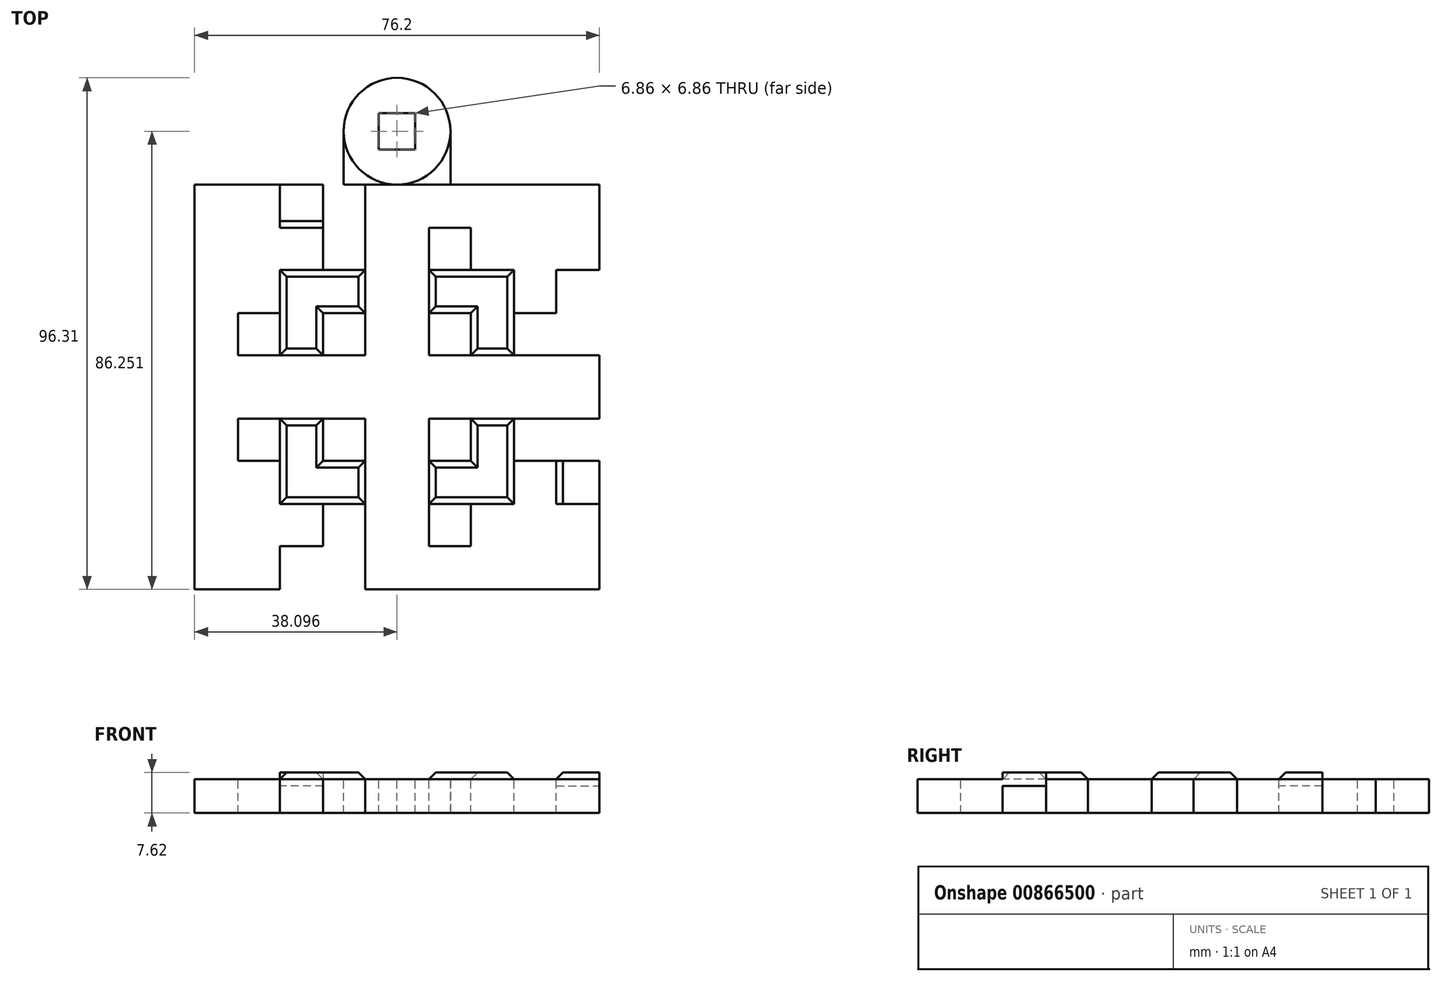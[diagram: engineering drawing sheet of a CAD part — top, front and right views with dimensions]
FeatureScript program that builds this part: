
annotation { "Feature Type Name" : "Feature", "Feature Type Description" : "" }
export const myFeature = defineFeature(function(context is Context, id is Id, definition is map)
    precondition{}
    {
        {
            var Q0;
            Q0=qCreatedBy(makeId("Top.planeOp"),FACE);
            var sketch = newSketch(context, id + "F0", { "sketchPlane" : qUnion([Q0])});
            skLineSegment(sketch, "E0.bottom", {"start": v(-34.48, 49.13) * mm, "end": v(41.72, 49.13) * mm});
            skLineSegment(sketch, "E0.top", {"start": v(-34.48, -27.07) * mm, "end": v(41.72, -27.07) * mm});
            skLineSegment(sketch, "E0.left", {"start": v(-34.48, 49.13) * mm, "end": v(-34.48, -27.07) * mm});
            skLineSegment(sketch, "E0.right", {"start": v(41.72, 49.13) * mm, "end": v(41.72, -27.07) * mm});
            skCircle(sketch, "E1", {"center": v(3.62, 59.18) * mm, "radius": 10.06 * mm});
            skLineSegment(sketch, "E2", {"start": v(3.62, -27.07) * mm, "end": v(3.62, 49.13) * mm, "construction": true});
            skPoint(sketch, "E3", {"position": v(3.62, 49.13) * mm});
            skSolve(sketch);
        }
        {
            var Q0;
            Q0=qSketchRegion(id+"F0",true);
            extrude(context, id + "F1", {"entities" : qUnion([Q0]), "depth" : 6.35 * mm, "offsetDistance" : 25.4 * mm});
        }
        {
            var Q0;
            Q0=makeQuery(id+"F1.opExtrude","CAP_FACE",FACE,{"disambiguationData":[OSD([sQuery(id+"F0.wireOp",EDGE,"E0.bottom"),sQuery(id+"F0.wireOp",EDGE,"E0.top"),sQuery(id+"F0.wireOp",EDGE,"E0.left"),sQuery(id+"F0.wireOp",EDGE,"E0.right")])],"isStart":false});
            var sketch = newSketch(context, id + "F2", { "sketchPlane" : qUnion([Q0])});
            skLineSegment(sketch, "E4.bottom", {"start": v(-34.48, 5.04) * mm, "end": v(41.72, 5.04) * mm});
            skLineSegment(sketch, "E4.top", {"start": v(-34.48, 17.01) * mm, "end": v(41.72, 17.01) * mm});
            skLineSegment(sketch, "E4.left", {"start": v(-34.48, 5.04) * mm, "end": v(-34.48, 17.01) * mm});
            skLineSegment(sketch, "E4.right", {"start": v(41.72, 5.04) * mm, "end": v(41.72, 17.01) * mm});
            skLineSegment(sketch, "E5.bottom", {"start": v(-34.48, 49.13) * mm, "end": v(-2.37, 49.13) * mm});
            skLineSegment(sketch, "E5.top", {"start": v(-34.48, -27.07) * mm, "end": v(-2.37, -27.07) * mm});
            skLineSegment(sketch, "E5.left", {"start": v(-34.48, 49.13) * mm, "end": v(-34.48, 17.01) * mm});
            skLineSegment(sketch, "E5.right", {"start": v(41.72, 49.13) * mm, "end": v(41.72, 17.01) * mm});
            skLineSegment(sketch, "E6", {"start": v(41.72, 17.01) * mm, "end": v(41.72, 5.04) * mm});
            skLineSegment(sketch, "E7", {"start": v(41.72, 5.04) * mm, "end": v(41.72, -27.07) * mm});
            skLineSegment(sketch, "E8.bottom", {"start": v(-2.37, 49.13) * mm, "end": v(9.6, 49.13) * mm});
            skLineSegment(sketch, "E8.top", {"start": v(-2.37, -27.07) * mm, "end": v(9.6, -27.07) * mm});
            skLineSegment(sketch, "E8.left", {"start": v(-2.37, 49.13) * mm, "end": v(-2.37, 49.13) * mm});
            skLineSegment(sketch, "E8.right", {"start": v(9.6, 49.13) * mm, "end": v(9.6, -27.07) * mm});
            skLineSegment(sketch, "E9", {"start": v(-2.37, 49.13) * mm, "end": v(-2.37, -27.07) * mm});
            skLineSegment(sketch, "E10", {"start": v(9.6, 49.13) * mm, "end": v(41.72, 49.13) * mm});
            skLineSegment(sketch, "E11", {"start": v(9.6, -27.07) * mm, "end": v(41.72, -27.07) * mm});
            skPoint(sketch, "E12.oppositeSnap0", {"position": v(25.66, 49.13) * mm});
            skLineSegment(sketch, "E12.bottom", {"start": v(-18.43, 49.13) * mm, "end": v(25.66, 49.13) * mm});
            skLineSegment(sketch, "E12.top", {"start": v(-18.43, 40.98) * mm, "end": v(25.66, 40.98) * mm});
            skLineSegment(sketch, "E12.left", {"start": v(-18.43, 49.13) * mm, "end": v(-18.43, 40.98) * mm});
            skLineSegment(sketch, "E12.right", {"start": v(25.66, 49.13) * mm, "end": v(25.66, 40.98) * mm});
            skPoint(sketch, "E13.oppositeSnap0", {"position": v(-18.43, -27.07) * mm});
            skLineSegment(sketch, "E13.bottom", {"start": v(25.66, -27.07) * mm, "end": v(-18.43, -27.07) * mm});
            skLineSegment(sketch, "E13.top", {"start": v(25.66, -18.92) * mm, "end": v(-18.43, -18.92) * mm});
            skLineSegment(sketch, "E13.left", {"start": v(25.66, -27.07) * mm, "end": v(25.66, -18.92) * mm});
            skLineSegment(sketch, "E13.right", {"start": v(-18.43, -27.07) * mm, "end": v(-18.43, -18.92) * mm});
            skPoint(sketch, "E14.oppositeSnap0", {"position": v(41.72, 33.07) * mm});
            skLineSegment(sketch, "E14.bottom", {"start": v(41.72, -11.02) * mm, "end": v(33.57, -11.02) * mm});
            skLineSegment(sketch, "E14.top", {"start": v(41.72, 33.07) * mm, "end": v(33.57, 33.07) * mm});
            skLineSegment(sketch, "E14.left", {"start": v(41.72, -11.02) * mm, "end": v(41.72, 33.07) * mm});
            skLineSegment(sketch, "E14.right", {"start": v(33.57, -11.02) * mm, "end": v(33.57, 33.07) * mm});
            skLineSegment(sketch, "E15", {"start": v(-34.48, 17.01) * mm, "end": v(-34.48, 5.04) * mm});
            skLineSegment(sketch, "E16", {"start": v(-34.48, 5.04) * mm, "end": v(-34.48, -27.07) * mm});
            skPoint(sketch, "E17.oppositeSnap0", {"position": v(-34.48, -11.02) * mm});
            skLineSegment(sketch, "E17.bottom", {"start": v(-34.48, 33.07) * mm, "end": v(-26.33, 33.07) * mm});
            skLineSegment(sketch, "E17.top", {"start": v(-34.48, -11.02) * mm, "end": v(-26.33, -11.02) * mm});
            skLineSegment(sketch, "E17.left", {"start": v(-34.48, 33.07) * mm, "end": v(-34.48, -11.02) * mm});
            skLineSegment(sketch, "E17.right", {"start": v(-26.33, 33.07) * mm, "end": v(-26.33, 24.92) * mm});
            skLineSegment(sketch, "E18.bottom", {"start": v(-18.43, 40.98) * mm, "end": v(-10.28, 40.98) * mm});
            skLineSegment(sketch, "E18.top", {"start": v(-18.43, 17.01) * mm, "end": v(-10.28, 17.01) * mm});
            skLineSegment(sketch, "E18.left", {"start": v(-18.43, 40.98) * mm, "end": v(-18.43, 17.01) * mm});
            skLineSegment(sketch, "E18.right", {"start": v(-10.28, 40.98) * mm, "end": v(-10.28, 17.01) * mm});
            skLineSegment(sketch, "E19.bottom", {"start": v(-26.33, 33.07) * mm, "end": v(-2.37, 33.07) * mm});
            skLineSegment(sketch, "E19.top", {"start": v(-26.33, 24.92) * mm, "end": v(-2.37, 24.92) * mm});
            skLineSegment(sketch, "E19.right", {"start": v(-2.37, 33.07) * mm, "end": v(-2.37, 24.92) * mm});
            skLineSegment(sketch, "E20", {"start": v(-26.33, 24.92) * mm, "end": v(-26.33, -11.02) * mm});
            skLineSegment(sketch, "E21.bottom", {"start": v(25.66, 40.98) * mm, "end": v(17.51, 40.98) * mm});
            skLineSegment(sketch, "E21.top", {"start": v(25.66, 17.01) * mm, "end": v(17.51, 17.01) * mm});
            skLineSegment(sketch, "E21.left", {"start": v(25.66, 40.98) * mm, "end": v(25.66, 17.01) * mm});
            skLineSegment(sketch, "E21.right", {"start": v(17.51, 40.98) * mm, "end": v(17.51, 17.01) * mm});
            skLineSegment(sketch, "E22.bottom", {"start": v(33.57, 33.07) * mm, "end": v(9.6, 33.07) * mm});
            skLineSegment(sketch, "E22.top", {"start": v(33.57, 24.92) * mm, "end": v(9.6, 24.92) * mm});
            skLineSegment(sketch, "E22.left", {"start": v(33.57, 33.07) * mm, "end": v(33.57, 24.92) * mm});
            skLineSegment(sketch, "E22.right", {"start": v(9.6, 33.07) * mm, "end": v(9.6, 24.92) * mm});
            skPoint(sketch, "E23.oppositeSnap0", {"position": v(-10.28, 29) * mm});
            skLineSegment(sketch, "E23.bottom", {"start": v(-18.43, -18.92) * mm, "end": v(-10.28, -18.92) * mm});
            skLineSegment(sketch, "E23.top", {"start": v(-18.43, 5.04) * mm, "end": v(-10.28, 5.04) * mm});
            skLineSegment(sketch, "E23.left", {"start": v(-18.43, -18.92) * mm, "end": v(-18.43, 5.04) * mm});
            skLineSegment(sketch, "E23.right", {"start": v(-10.28, -18.92) * mm, "end": v(-10.28, 5.04) * mm});
            skLineSegment(sketch, "E24.bottom", {"start": v(25.66, -18.92) * mm, "end": v(17.51, -18.92) * mm});
            skLineSegment(sketch, "E24.top", {"start": v(25.66, 5.04) * mm, "end": v(17.51, 5.04) * mm});
            skLineSegment(sketch, "E24.left", {"start": v(25.66, -18.92) * mm, "end": v(25.66, 5.04) * mm});
            skLineSegment(sketch, "E24.right", {"start": v(17.51, -18.92) * mm, "end": v(17.51, 5.04) * mm});
            skLineSegment(sketch, "E25.bottom", {"start": v(-26.33, -11.02) * mm, "end": v(-2.37, -11.02) * mm});
            skLineSegment(sketch, "E25.top", {"start": v(-26.33, -2.87) * mm, "end": v(-2.37, -2.87) * mm});
            skLineSegment(sketch, "E25.left", {"start": v(-26.33, -11.02) * mm, "end": v(-26.33, -2.87) * mm});
            skLineSegment(sketch, "E25.right", {"start": v(-2.37, -11.02) * mm, "end": v(-2.37, -2.87) * mm});
            skLineSegment(sketch, "E26.bottom", {"start": v(9.6, -11.02) * mm, "end": v(33.57, -11.02) * mm});
            skLineSegment(sketch, "E26.top", {"start": v(9.6, -2.87) * mm, "end": v(33.57, -2.87) * mm});
            skLineSegment(sketch, "E26.left", {"start": v(9.6, -11.02) * mm, "end": v(9.6, -2.87) * mm});
            skLineSegment(sketch, "E26.right", {"start": v(33.57, -11.02) * mm, "end": v(33.57, -2.87) * mm});
            skLineSegment(sketch, "E27.bottom", {"start": v(-18.43, 49.13) * mm, "end": v(-10.28, 49.13) * mm});
            skLineSegment(sketch, "E27.right", {"start": v(-10.28, 49.13) * mm, "end": v(-10.28, 40.98) * mm});
            skLineSegment(sketch, "E28.bottom", {"start": v(17.51, 40.98) * mm, "end": v(25.66, 40.98) * mm});
            skLineSegment(sketch, "E28.top", {"start": v(17.51, 49.13) * mm, "end": v(25.66, 49.13) * mm});
            skLineSegment(sketch, "E28.left", {"start": v(17.51, 40.98) * mm, "end": v(17.51, 49.13) * mm});
            skLineSegment(sketch, "E28.right", {"start": v(25.66, 40.98) * mm, "end": v(25.66, 49.13) * mm});
            skLineSegment(sketch, "E29.bottom", {"start": v(33.57, 24.92) * mm, "end": v(41.72, 24.92) * mm});
            skLineSegment(sketch, "E29.top", {"start": v(33.57, 17.01) * mm, "end": v(41.72, 17.01) * mm});
            skLineSegment(sketch, "E29.left", {"start": v(33.57, 24.92) * mm, "end": v(33.57, 17.01) * mm});
            skLineSegment(sketch, "E29.right", {"start": v(41.72, 24.92) * mm, "end": v(41.72, 17.01) * mm});
            skLineSegment(sketch, "E30.bottom", {"start": v(-26.33, 24.92) * mm, "end": v(-34.48, 24.92) * mm});
            skLineSegment(sketch, "E30.top", {"start": v(-26.33, 33.07) * mm, "end": v(-34.48, 33.07) * mm});
            skLineSegment(sketch, "E30.left", {"start": v(-26.33, 24.92) * mm, "end": v(-26.33, 33.07) * mm});
            skLineSegment(sketch, "E30.right", {"start": v(-34.48, 24.92) * mm, "end": v(-34.48, 33.07) * mm});
            skLineSegment(sketch, "E31.top", {"start": v(-34.48, -2.87) * mm, "end": v(-26.33, -2.87) * mm});
            skLineSegment(sketch, "E31.left", {"start": v(-34.48, -11.02) * mm, "end": v(-34.48, -2.87) * mm});
            skLineSegment(sketch, "E32.top", {"start": v(-18.43, -27.07) * mm, "end": v(-10.28, -27.07) * mm});
            skLineSegment(sketch, "E32.left", {"start": v(-18.43, -18.92) * mm, "end": v(-18.43, -27.07) * mm});
            skLineSegment(sketch, "E32.right", {"start": v(-10.28, -18.92) * mm, "end": v(-10.28, -27.07) * mm});
            skLineSegment(sketch, "E33.bottom", {"start": v(17.51, -18.92) * mm, "end": v(25.66, -18.92) * mm});
            skLineSegment(sketch, "E33.top", {"start": v(17.51, -27.07) * mm, "end": v(25.66, -27.07) * mm});
            skLineSegment(sketch, "E33.left", {"start": v(17.51, -18.92) * mm, "end": v(17.51, -27.07) * mm});
            skLineSegment(sketch, "E33.right", {"start": v(25.66, -18.92) * mm, "end": v(25.66, -27.07) * mm});
            skLineSegment(sketch, "E34.bottom", {"start": v(33.57, -11.02) * mm, "end": v(41.72, -11.02) * mm});
            skLineSegment(sketch, "E34.top", {"start": v(33.57, -2.87) * mm, "end": v(41.72, -2.87) * mm});
            skLineSegment(sketch, "E34.right", {"start": v(41.72, -11.02) * mm, "end": v(41.72, -2.87) * mm});
            skText(sketch, "E35", { "text": "C.C.\n", "fontName": "OpenSans-Regular.ttf"});
            const initialGuessF2  = {"E35": [0, -0.02441, 1, 0, 0.00324]};
            skSetInitialGuess(sketch, initialGuessF2);
            skSolve(sketch);
        }
        {
            var Q0;
            Q0=makeQuery(id+"F2.imprint","IMPRINT",FACE,{"disambiguationData":[TD([[makeQuery(id+"F2.imprint","IMPRINT",EDGE,{"derivedFrom":sQuery(id+"F2.wireOp",EDGE,"E5.bottom")}),-1.0]])]});
            var Q1;
            Q1=makeQuery(id+"F2.imprint","IMPRINT",FACE,{"disambiguationData":[TD([[makeQuery(id+"F2.imprint","IMPRINT",EDGE,{"derivedFrom":sQuery(id+"F2.wireOp",EDGE,"E5.right")}),-1.0]])]});
            var Q2;
            Q2=makeQuery(id+"F2.imprint","IMPRINT",FACE,{"disambiguationData":[TD([[makeQuery(id+"F2.imprint","IMPRINT",EDGE,{"derivedFrom":sQuery(id+"F2.wireOp",EDGE,"E7")}),-1.0]])]});
            var Q3;
            Q3=makeQuery(id+"F2.imprint","IMPRINT",FACE,{"disambiguationData":[TD([[makeQuery(id+"F2.imprint","IMPRINT",EDGE,{"derivedFrom":sQuery(id+"F2.wireOp",EDGE,"E5.top")}),1.0]])]});
            var Q4;
            {var subQ1=sQuery(id+"F2.wireOp",EDGE,"E4.bottom");var subQ3=sQuery(id+"F2.wireOp",EDGE,"E20");var subQ4=makeQuery(id+"F2.imprint","INTERSECT",VERTEX,{"derivedFrom":[subQ1,subQ3]});Q4=makeQuery(id+"F2.imprint","IMPRINT",FACE,{"disambiguationData":[TD([[makeQuery(id+"F2.imprint","IMPRINT",EDGE,{"disambiguationData":[TD([[subQ4,-1.0]])],"derivedFrom":subQ1}),-1.0]])]});}
            var Q5;
            {var subQ1=sQuery(id+"F2.wireOp",EDGE,"E4.top");var subQ3=sQuery(id+"F2.wireOp",EDGE,"E20");var subQ4=makeQuery(id+"F2.imprint","INTERSECT",VERTEX,{"derivedFrom":[subQ1,subQ3]});Q5=makeQuery(id+"F2.imprint","IMPRINT",FACE,{"disambiguationData":[TD([[makeQuery(id+"F2.imprint","IMPRINT",EDGE,{"disambiguationData":[TD([[subQ4,-1.0]])],"derivedFrom":subQ1}),1.0]])]});}
            var Q6;
            {var subQ1=sQuery(id+"F2.wireOp",EDGE,"E9");var subQ3=sQuery(id+"F2.wireOp",EDGE,"E12.top");var subQ4=makeQuery(id+"F2.imprint","INTERSECT",VERTEX,{"derivedFrom":[subQ1,subQ3]});Q6=makeQuery(id+"F2.imprint","IMPRINT",FACE,{"disambiguationData":[TD([[makeQuery(id+"F2.imprint","IMPRINT",EDGE,{"disambiguationData":[TD([[subQ4,-1.0]])],"derivedFrom":subQ1}),-1.0]])]});}
            var Q7;
            {var subQ1=sQuery(id+"F2.wireOp",EDGE,"E4.top");var subQ3=sQuery(id+"F2.wireOp",EDGE,"E9");var subQ4=makeQuery(id+"F2.imprint","INTERSECT",VERTEX,{"derivedFrom":[subQ1,subQ3]});Q7=makeQuery(id+"F2.imprint","IMPRINT",FACE,{"disambiguationData":[TD([[makeQuery(id+"F2.imprint","IMPRINT",EDGE,{"disambiguationData":[TD([[subQ4,1.0]])],"derivedFrom":subQ1}),1.0]])]});}
            var Q8;
            {var subQ1=sQuery(id+"F2.wireOp",EDGE,"E4.bottom");var subQ3=sQuery(id+"F2.wireOp",EDGE,"E9");var subQ4=makeQuery(id+"F2.imprint","INTERSECT",VERTEX,{"derivedFrom":[subQ1,subQ3]});Q8=makeQuery(id+"F2.imprint","IMPRINT",FACE,{"disambiguationData":[TD([[makeQuery(id+"F2.imprint","IMPRINT",EDGE,{"disambiguationData":[TD([[subQ4,1.0]])],"derivedFrom":subQ1}),-1.0]])]});}
            var Q9;
            {var subQ1=sQuery(id+"F2.wireOp",EDGE,"E9");var subQ3=sQuery(id+"F2.wireOp",EDGE,"E13.top");var subQ4=makeQuery(id+"F2.imprint","INTERSECT",VERTEX,{"derivedFrom":[subQ1,subQ3]});Q9=makeQuery(id+"F2.imprint","IMPRINT",FACE,{"disambiguationData":[TD([[makeQuery(id+"F2.imprint","IMPRINT",EDGE,{"disambiguationData":[TD([[subQ4,1.0]])],"derivedFrom":subQ1}),-1.0]])]});}
            var Q10;
            {var subQ1=sQuery(id+"F2.wireOp",EDGE,"E8.right");var subQ3=sQuery(id+"F2.wireOp",EDGE,"E13.top");var subQ4=makeQuery(id+"F2.imprint","INTERSECT",VERTEX,{"derivedFrom":[subQ1,subQ3]});Q10=makeQuery(id+"F2.imprint","IMPRINT",FACE,{"disambiguationData":[TD([[makeQuery(id+"F2.imprint","IMPRINT",EDGE,{"disambiguationData":[TD([[subQ4,1.0]])],"derivedFrom":subQ1}),1.0]])]});}
            var Q11;
            {var subQ1=sQuery(id+"F2.wireOp",EDGE,"E4.bottom");var subQ3=sQuery(id+"F2.wireOp",EDGE,"E8.right");var subQ4=makeQuery(id+"F2.imprint","INTERSECT",VERTEX,{"derivedFrom":[subQ1,subQ3]});Q11=makeQuery(id+"F2.imprint","IMPRINT",FACE,{"disambiguationData":[TD([[makeQuery(id+"F2.imprint","IMPRINT",EDGE,{"disambiguationData":[TD([[subQ4,-1.0]])],"derivedFrom":subQ1}),-1.0]])]});}
            var Q12;
            {var subQ1=sQuery(id+"F2.wireOp",EDGE,"E4.bottom");var subQ3=sQuery(id+"F2.wireOp",EDGE,"E14.right");var subQ4=makeQuery(id+"F2.imprint","INTERSECT",VERTEX,{"derivedFrom":[subQ1,subQ3]});Q12=makeQuery(id+"F2.imprint","IMPRINT",FACE,{"disambiguationData":[TD([[makeQuery(id+"F2.imprint","IMPRINT",EDGE,{"disambiguationData":[TD([[subQ4,1.0]])],"derivedFrom":subQ1}),-1.0]])]});}
            var Q13;
            {var subQ1=sQuery(id+"F2.wireOp",EDGE,"E4.top");var subQ3=sQuery(id+"F2.wireOp",EDGE,"E14.right");var subQ4=makeQuery(id+"F2.imprint","INTERSECT",VERTEX,{"derivedFrom":[subQ1,subQ3]});Q13=makeQuery(id+"F2.imprint","IMPRINT",FACE,{"disambiguationData":[TD([[makeQuery(id+"F2.imprint","IMPRINT",EDGE,{"disambiguationData":[TD([[subQ4,1.0]])],"derivedFrom":subQ1}),1.0]])]});}
            var Q14;
            {var subQ1=sQuery(id+"F2.wireOp",EDGE,"E4.top");var subQ3=sQuery(id+"F2.wireOp",EDGE,"E8.right");var subQ4=makeQuery(id+"F2.imprint","INTERSECT",VERTEX,{"derivedFrom":[subQ1,subQ3]});Q14=makeQuery(id+"F2.imprint","IMPRINT",FACE,{"disambiguationData":[TD([[makeQuery(id+"F2.imprint","IMPRINT",EDGE,{"disambiguationData":[TD([[subQ4,-1.0]])],"derivedFrom":subQ1}),1.0]])]});}
            var Q15;
            {var subQ1=sQuery(id+"F2.wireOp",EDGE,"E8.right");var subQ3=sQuery(id+"F2.wireOp",EDGE,"E12.top");var subQ4=makeQuery(id+"F2.imprint","INTERSECT",VERTEX,{"derivedFrom":[subQ1,subQ3]});Q15=makeQuery(id+"F2.imprint","IMPRINT",FACE,{"disambiguationData":[TD([[makeQuery(id+"F2.imprint","IMPRINT",EDGE,{"disambiguationData":[TD([[subQ4,-1.0]])],"derivedFrom":subQ1}),1.0]])]});}
            var Q16;
            Q16=qSketchRegion(id+"F6",true);
            extrude(context, id + "F3", {"entities" : qUnion([Q0, Q1, Q2, Q3, Q4, Q5, Q6, Q7, Q8, Q9, Q10, Q11, Q12, Q13, Q14, Q15, Q16]), "operationType" : NewBodyOperationType.REMOVE, "oppositeDirection" : true, "depth" : 25.4 * mm, "offsetDistance" : 25.4 * mm});
        }
        {
            var Q0;
            Q0=makeQuery(id+"F1.opExtrude","CAP_FACE",FACE,{"disambiguationData":[OSD([sQuery(id+"F0.wireOp",EDGE,"E1")])],"isStart":false});
            var sketch = newSketch(context, id + "F4", { "sketchPlane" : qUnion([Q0])});
            skLineSegment(sketch, "E36.bottom", {"start": v(7.04, 55.75) * mm, "end": v(0.19, 55.75) * mm});
            skLineSegment(sketch, "E36.top", {"start": v(7.04, 62.61) * mm, "end": v(0.19, 62.61) * mm});
            skLineSegment(sketch, "E36.left", {"start": v(7.04, 55.75) * mm, "end": v(7.04, 62.61) * mm});
            skLineSegment(sketch, "E36.right", {"start": v(0.19, 55.75) * mm, "end": v(0.19, 62.61) * mm});
            skPoint(sketch, "E36.middle", {"position": v(3.62, 59.18) * mm});
            skSolve(sketch);
        }
        {
            var Q0;
            Q0=makeQuery(id+"F4.imprint","IMPRINT",FACE,{"disambiguationData":[TD([[makeQuery(id+"F4.imprint","IMPRINT",EDGE,{"derivedFrom":sQuery(id+"F4.wireOp",EDGE,"E36.bottom")}),-1.0]])]});
            var Q1;
            Q1=qSketchRegion(id+"F6",true);
            extrude(context, id + "F5", {"entities" : qUnion([Q0, Q1]), "operationType" : NewBodyOperationType.REMOVE, "oppositeDirection" : true, "depth" : 25.4 * mm, "offsetDistance" : 25.4 * mm});
        }
        {
            var Q0;
            Q0=makeQuery(id+"F1.opExtrude","CAP_FACE",FACE,{"disambiguationData":[OSD([sQuery(id+"F0.wireOp",EDGE,"E0.bottom"),sQuery(id+"F0.wireOp",EDGE,"E0.top"),sQuery(id+"F0.wireOp",EDGE,"E0.left"),sQuery(id+"F0.wireOp",EDGE,"E0.right")])],"isStart":false});
            var sketch = newSketch(context, id + "F6", { "sketchPlane" : qUnion([Q0])});
            skLineSegment(sketch, "E37.bottom", {"start": v(-26.33, 24.92) * mm, "end": v(-34.48, 24.92) * mm});
            skLineSegment(sketch, "E37.top", {"start": v(-26.33, 33.07) * mm, "end": v(-34.48, 33.07) * mm});
            skLineSegment(sketch, "E37.left", {"start": v(-26.33, 24.92) * mm, "end": v(-26.33, 33.07) * mm});
            skLineSegment(sketch, "E37.right", {"start": v(-34.48, 24.92) * mm, "end": v(-34.48, 33.07) * mm});
            skLineSegment(sketch, "E38.bottom", {"start": v(-26.33, -2.87) * mm, "end": v(-34.48, -2.87) * mm});
            skLineSegment(sketch, "E38.top", {"start": v(-26.33, -11.02) * mm, "end": v(-34.48, -11.02) * mm});
            skLineSegment(sketch, "E38.left", {"start": v(-26.33, -2.87) * mm, "end": v(-26.33, -11.02) * mm});
            skLineSegment(sketch, "E38.right", {"start": v(-34.48, -2.87) * mm, "end": v(-34.48, -11.02) * mm});
            skLineSegment(sketch, "E39.bottom", {"start": v(-10.28, 40.98) * mm, "end": v(-18.43, 40.98) * mm});
            skLineSegment(sketch, "E39.top", {"start": v(-10.28, 49.13) * mm, "end": v(-18.43, 49.13) * mm});
            skLineSegment(sketch, "E39.left", {"start": v(-10.28, 40.98) * mm, "end": v(-10.28, 49.13) * mm});
            skLineSegment(sketch, "E39.right", {"start": v(-18.43, 40.98) * mm, "end": v(-18.43, 49.13) * mm});
            skLineSegment(sketch, "E40.bottom", {"start": v(17.51, 40.98) * mm, "end": v(25.66, 40.98) * mm});
            skLineSegment(sketch, "E40.top", {"start": v(17.51, 49.13) * mm, "end": v(25.66, 49.13) * mm});
            skLineSegment(sketch, "E40.left", {"start": v(17.51, 40.98) * mm, "end": v(17.51, 49.13) * mm});
            skLineSegment(sketch, "E40.right", {"start": v(25.66, 40.98) * mm, "end": v(25.66, 49.13) * mm});
            skLineSegment(sketch, "E41.bottom", {"start": v(33.57, 24.92) * mm, "end": v(41.72, 24.92) * mm});
            skLineSegment(sketch, "E41.top", {"start": v(33.57, 33.07) * mm, "end": v(41.72, 33.07) * mm});
            skLineSegment(sketch, "E41.left", {"start": v(33.57, 24.92) * mm, "end": v(33.57, 33.07) * mm});
            skLineSegment(sketch, "E41.right", {"start": v(41.72, 24.92) * mm, "end": v(41.72, 33.07) * mm});
            skLineSegment(sketch, "E42.bottom", {"start": v(33.57, -2.87) * mm, "end": v(41.72, -2.87) * mm});
            skLineSegment(sketch, "E42.top", {"start": v(33.57, -11.02) * mm, "end": v(41.72, -11.02) * mm});
            skLineSegment(sketch, "E42.left", {"start": v(33.57, -2.87) * mm, "end": v(33.57, -11.02) * mm});
            skLineSegment(sketch, "E42.right", {"start": v(41.72, -2.87) * mm, "end": v(41.72, -11.02) * mm});
            skLineSegment(sketch, "E43.bottom", {"start": v(17.51, -18.92) * mm, "end": v(25.66, -18.92) * mm});
            skLineSegment(sketch, "E43.top", {"start": v(17.51, -27.07) * mm, "end": v(25.66, -27.07) * mm});
            skLineSegment(sketch, "E43.left", {"start": v(17.51, -18.92) * mm, "end": v(17.51, -27.07) * mm});
            skLineSegment(sketch, "E43.right", {"start": v(25.66, -18.92) * mm, "end": v(25.66, -27.07) * mm});
            skLineSegment(sketch, "E44.bottom", {"start": v(-10.28, -18.92) * mm, "end": v(-18.43, -18.92) * mm});
            skLineSegment(sketch, "E44.top", {"start": v(-10.28, -27.07) * mm, "end": v(-18.43, -27.07) * mm});
            skLineSegment(sketch, "E44.left", {"start": v(-10.28, -18.92) * mm, "end": v(-10.28, -27.07) * mm});
            skLineSegment(sketch, "E44.right", {"start": v(-18.43, -18.92) * mm, "end": v(-18.43, -27.07) * mm});
            skLineSegment(sketch, "E45.bottom", {"start": v(-26.33, 33.07) * mm, "end": v(-2.37, 33.07) * mm});
            skLineSegment(sketch, "E45.top", {"start": v(-26.33, 24.92) * mm, "end": v(-2.37, 24.92) * mm});
            skLineSegment(sketch, "E45.left", {"start": v(-26.33, 33.07) * mm, "end": v(-26.33, 24.92) * mm});
            skLineSegment(sketch, "E45.right", {"start": v(-2.37, 33.07) * mm, "end": v(-2.37, 24.92) * mm});
            skLineSegment(sketch, "E46.top", {"start": v(-10.28, 17.01) * mm, "end": v(-18.43, 17.01) * mm});
            skLineSegment(sketch, "E46.left", {"start": v(-10.28, 40.98) * mm, "end": v(-10.28, 17.01) * mm});
            skLineSegment(sketch, "E46.right", {"start": v(-18.43, 40.98) * mm, "end": v(-18.43, 17.01) * mm});
            skLineSegment(sketch, "E47.bottom", {"start": v(-18.43, 5.04) * mm, "end": v(-10.28, 5.04) * mm});
            skLineSegment(sketch, "E47.top", {"start": v(-18.43, -18.92) * mm, "end": v(-10.28, -18.92) * mm});
            skLineSegment(sketch, "E47.left", {"start": v(-18.43, 5.04) * mm, "end": v(-18.43, -18.92) * mm});
            skLineSegment(sketch, "E47.right", {"start": v(-10.28, 5.04) * mm, "end": v(-10.28, -18.92) * mm});
            skLineSegment(sketch, "E48.bottom", {"start": v(-26.33, -11.02) * mm, "end": v(-2.37, -11.02) * mm});
            skLineSegment(sketch, "E48.top", {"start": v(-26.33, -2.87) * mm, "end": v(-2.37, -2.87) * mm});
            skLineSegment(sketch, "E48.left", {"start": v(-26.33, -11.02) * mm, "end": v(-26.33, -2.87) * mm});
            skLineSegment(sketch, "E48.right", {"start": v(-2.37, -11.02) * mm, "end": v(-2.37, -2.87) * mm});
            skLineSegment(sketch, "E49.bottom", {"start": v(9.6, -2.87) * mm, "end": v(33.57, -2.87) * mm});
            skLineSegment(sketch, "E49.top", {"start": v(9.6, -11.02) * mm, "end": v(33.57, -11.02) * mm});
            skLineSegment(sketch, "E49.left", {"start": v(9.6, -2.87) * mm, "end": v(9.6, -11.02) * mm});
            skLineSegment(sketch, "E50.bottom", {"start": v(25.66, -18.92) * mm, "end": v(17.51, -18.92) * mm});
            skLineSegment(sketch, "E50.top", {"start": v(25.66, 5.04) * mm, "end": v(17.51, 5.04) * mm});
            skLineSegment(sketch, "E50.left", {"start": v(25.66, -18.92) * mm, "end": v(25.66, 5.04) * mm});
            skLineSegment(sketch, "E50.right", {"start": v(17.51, -18.92) * mm, "end": v(17.51, 5.04) * mm});
            skLineSegment(sketch, "E51.bottom", {"start": v(17.51, 17.01) * mm, "end": v(25.66, 17.01) * mm});
            skLineSegment(sketch, "E51.left", {"start": v(17.51, 17.01) * mm, "end": v(17.51, 40.98) * mm});
            skLineSegment(sketch, "E51.right", {"start": v(25.66, 17.01) * mm, "end": v(25.66, 40.98) * mm});
            skLineSegment(sketch, "E52.bottom", {"start": v(9.6, 33.07) * mm, "end": v(33.57, 33.07) * mm});
            skLineSegment(sketch, "E52.top", {"start": v(9.6, 24.92) * mm, "end": v(33.57, 24.92) * mm});
            skLineSegment(sketch, "E52.left", {"start": v(9.6, 33.07) * mm, "end": v(9.6, 24.92) * mm});
            skLineSegment(sketch, "E52.right", {"start": v(33.57, 33.07) * mm, "end": v(33.57, 24.92) * mm});
            skSolve(sketch);
        }
        {
            var Q0;
            {var subQ3=sQuery(id+"F6.wireOp",EDGE,"E45.left");Q0=makeQuery(id+"F6.imprint","IMPRINT",FACE,{"disambiguationData":[TD([[makeQuery(id+"F6.imprint","IMPRINT",EDGE,{"derivedFrom":subQ3}),1.0]])]});}
            var Q1;
            {var subQ1=sQuery(id+"F6.wireOp",EDGE,"E45.bottom");var subQ3=sQuery(id+"F6.wireOp",EDGE,"E46.left");var subQ4=makeQuery(id+"F6.imprint","INTERSECT",VERTEX,{"derivedFrom":[subQ1,subQ3]});Q1=makeQuery(id+"F6.imprint","IMPRINT",FACE,{"disambiguationData":[TD([[makeQuery(id+"F6.imprint","IMPRINT",EDGE,{"disambiguationData":[TD([[subQ4,1.0]])],"derivedFrom":subQ1}),-1.0]])]});}
            var Q2;
            {var subQ5=sQuery(id+"F6.wireOp",EDGE,"E39.bottom");Q2=makeQuery(id+"F6.imprint","IMPRINT",FACE,{"disambiguationData":[TD([[makeQuery(id+"F6.imprint","IMPRINT",EDGE,{"derivedFrom":subQ5}),1.0]])]});}
            var Q3;
            {var subQ0=sQuery(id+"F6.wireOp",EDGE,"E45.right");Q3=makeQuery(id+"F6.imprint","IMPRINT",FACE,{"disambiguationData":[TD([[makeQuery(id+"F6.imprint","IMPRINT",EDGE,{"derivedFrom":subQ0}),-1.0]])]});}
            var Q4;
            {var subQ5=sQuery(id+"F6.wireOp",EDGE,"E46.top");Q4=makeQuery(id+"F6.imprint","IMPRINT",FACE,{"disambiguationData":[TD([[makeQuery(id+"F6.imprint","IMPRINT",EDGE,{"derivedFrom":subQ5}),-1.0]])]});}
            var Q5;
            {var subQ5=sQuery(id+"F6.wireOp",EDGE,"E52.left");Q5=makeQuery(id+"F6.imprint","IMPRINT",FACE,{"disambiguationData":[TD([[makeQuery(id+"F6.imprint","IMPRINT",EDGE,{"derivedFrom":subQ5}),1.0]])]});}
            var Q6;
            {var subQ5=sQuery(id+"F6.wireOp",EDGE,"E52.right");Q6=makeQuery(id+"F6.imprint","IMPRINT",FACE,{"disambiguationData":[TD([[makeQuery(id+"F6.imprint","IMPRINT",EDGE,{"derivedFrom":subQ5}),-1.0]])]});}
            var Q7;
            {var subQ0=sQuery(id+"F6.wireOp",EDGE,"E52.bottom");var subQ1=sQuery(id+"F6.wireOp",EDGE,"E51.left");var subQ2=makeQuery(id+"F6.imprint","INTERSECT",VERTEX,{"derivedFrom":[subQ1,subQ0]});var subQ3=sQuery(id+"F6.wireOp",EDGE,"E52.top");var subQ4=makeQuery(id+"F6.imprint","INTERSECT",VERTEX,{"derivedFrom":[subQ1,subQ3]});Q7=makeQuery(id+"F6.imprint","IMPRINT",FACE,{"disambiguationData":[TD([[makeQuery(id+"F6.imprint","IMPRINT",EDGE,{"disambiguationData":[TD([[subQ2,1.0],[subQ4,-1.0]])],"derivedFrom":subQ1}),-1.0]])]});}
            var Q8;
            {var subQ0=sQuery(id+"F6.wireOp",EDGE,"E40.bottom");Q8=makeQuery(id+"F6.imprint","IMPRINT",FACE,{"disambiguationData":[TD([[makeQuery(id+"F6.imprint","IMPRINT",EDGE,{"derivedFrom":subQ0}),-1.0]])]});}
            var Q9;
            {var subQ0=sQuery(id+"F6.wireOp",EDGE,"E51.bottom");Q9=makeQuery(id+"F6.imprint","IMPRINT",FACE,{"disambiguationData":[TD([[makeQuery(id+"F6.imprint","IMPRINT",EDGE,{"derivedFrom":subQ0}),1.0]])]});}
            var Q10;
            {var subQ0=sQuery(id+"F6.wireOp",EDGE,"E47.bottom");Q10=makeQuery(id+"F6.imprint","IMPRINT",FACE,{"disambiguationData":[TD([[makeQuery(id+"F6.imprint","IMPRINT",EDGE,{"derivedFrom":subQ0}),-1.0]])]});}
            var Q11;
            {var subQ0=sQuery(id+"F6.wireOp",EDGE,"E48.bottom");var subQ1=sQuery(id+"F6.wireOp",EDGE,"E47.left");var subQ2=makeQuery(id+"F6.imprint","INTERSECT",VERTEX,{"derivedFrom":[subQ1,subQ0]});Q11=makeQuery(id+"F6.imprint","IMPRINT",FACE,{"disambiguationData":[TD([[makeQuery(id+"F6.imprint","IMPRINT",EDGE,{"disambiguationData":[TD([[subQ2,1.0]])],"derivedFrom":subQ1}),1.0]])]});}
            var Q12;
            {var subQ0=sQuery(id+"F6.wireOp",EDGE,"E47.top");Q12=makeQuery(id+"F6.imprint","IMPRINT",FACE,{"disambiguationData":[TD([[makeQuery(id+"F6.imprint","IMPRINT",EDGE,{"derivedFrom":subQ0}),1.0]])]});}
            var Q13;
            {var subQ5=sQuery(id+"F6.wireOp",EDGE,"E48.left");Q13=makeQuery(id+"F6.imprint","IMPRINT",FACE,{"disambiguationData":[TD([[makeQuery(id+"F6.imprint","IMPRINT",EDGE,{"derivedFrom":subQ5}),-1.0]])]});}
            var Q14;
            {var subQ5=sQuery(id+"F6.wireOp",EDGE,"E48.right");Q14=makeQuery(id+"F6.imprint","IMPRINT",FACE,{"disambiguationData":[TD([[makeQuery(id+"F6.imprint","IMPRINT",EDGE,{"derivedFrom":subQ5}),1.0]])]});}
            var Q15;
            {var subQ0=sQuery(id+"F6.wireOp",EDGE,"E49.left");Q15=makeQuery(id+"F6.imprint","IMPRINT",FACE,{"disambiguationData":[TD([[makeQuery(id+"F6.imprint","IMPRINT",EDGE,{"derivedFrom":subQ0}),1.0]])]});}
            var Q16;
            {var subQ0=sQuery(id+"F6.wireOp",EDGE,"E50.left");var subQ1=sQuery(id+"F6.wireOp",EDGE,"E49.bottom");var subQ2=makeQuery(id+"F6.imprint","INTERSECT",VERTEX,{"derivedFrom":[subQ1,subQ0]});Q16=makeQuery(id+"F6.imprint","IMPRINT",FACE,{"disambiguationData":[TD([[makeQuery(id+"F6.imprint","IMPRINT",EDGE,{"disambiguationData":[TD([[subQ2,1.0]])],"derivedFrom":subQ1}),-1.0]])]});}
            var Q17;
            {var subQ0=sQuery(id+"F6.wireOp",EDGE,"E42.left");Q17=makeQuery(id+"F6.imprint","IMPRINT",FACE,{"disambiguationData":[TD([[makeQuery(id+"F6.imprint","IMPRINT",EDGE,{"derivedFrom":subQ0}),-1.0]])]});}
            var Q18;
            {var subQ5=sQuery(id+"F6.wireOp",EDGE,"E50.bottom");Q18=makeQuery(id+"F6.imprint","IMPRINT",FACE,{"disambiguationData":[TD([[makeQuery(id+"F6.imprint","IMPRINT",EDGE,{"derivedFrom":subQ5}),-1.0]])]});}
            var Q19;
            {var subQ5=sQuery(id+"F6.wireOp",EDGE,"E50.top");Q19=makeQuery(id+"F6.imprint","IMPRINT",FACE,{"disambiguationData":[TD([[makeQuery(id+"F6.imprint","IMPRINT",EDGE,{"derivedFrom":subQ5}),1.0]])]});}
            extrude(context, id + "F7", {"entities" : qUnion([Q0, Q1, Q2, Q3, Q4, Q5, Q6, Q7, Q8, Q9, Q10, Q11, Q12, Q13, Q14, Q15, Q16, Q17, Q18, Q19]), "operationType" : NewBodyOperationType.ADD, "depth" : 2.54 * mm, "offsetDistance" : 25.4 * mm, "symmetric" : true});
        }
        {
            var Q0;
            {var subQ0=sQuery(id+"F6.wireOp",EDGE,"E45.bottom");Q0=makeQuery(id+"F7.opExtrude","CAP_EDGE",EDGE,{"disambiguationData":[OSD([subQ0]),TDD([makeQuery(id+"F6.imprint","IMPRINT",EDGE,{"disambiguationData":[TD([[makeQuery(id+"F6.imprint","INTERSECT",VERTEX,{"derivedFrom":[sQuery(id+"F6.wireOp",EDGE,"E37.top"),subQ0,sQuery(id+"F6.wireOp",EDGE,"E45.left")]}),1.0]])],"derivedFrom":subQ0})])],"isStart":false});}
            var Q1;
            {var subQ0=sQuery(id+"F6.wireOp",EDGE,"E46.right");Q1=makeQuery(id+"F7.opExtrude","CAP_EDGE",EDGE,{"disambiguationData":[OSD([subQ0]),TDD([makeQuery(id+"F6.imprint","IMPRINT",EDGE,{"disambiguationData":[TD([[makeQuery(id+"F6.imprint","INTERSECT",VERTEX,{"derivedFrom":[sQuery(id+"F6.wireOp",EDGE,"E45.bottom"),subQ0]}),1.0]])],"derivedFrom":subQ0})])],"isStart":false});}
            var Q2;
            Q2=makeQuery(id+"F7.opExtrude","CAP_EDGE",EDGE,{"disambiguationData":[OSD([sQuery(id+"F6.wireOp",EDGE,"E39.bottom")])],"isStart":false});
            var Q3;
            {var subQ0=sQuery(id+"F6.wireOp",EDGE,"E46.left");Q3=makeQuery(id+"F7.opExtrude","CAP_EDGE",EDGE,{"disambiguationData":[OSD([subQ0]),TDD([makeQuery(id+"F6.imprint","IMPRINT",EDGE,{"disambiguationData":[TD([[makeQuery(id+"F6.imprint","INTERSECT",VERTEX,{"derivedFrom":[sQuery(id+"F6.wireOp",EDGE,"E45.bottom"),subQ0]}),1.0]])],"derivedFrom":subQ0})])],"isStart":false});}
            var Q4;
            {var subQ0=sQuery(id+"F6.wireOp",EDGE,"E45.bottom");Q4=makeQuery(id+"F7.opExtrude","CAP_EDGE",EDGE,{"disambiguationData":[OSD([subQ0]),TDD([makeQuery(id+"F6.imprint","IMPRINT",EDGE,{"disambiguationData":[TD([[makeQuery(id+"F6.imprint","INTERSECT",VERTEX,{"derivedFrom":[subQ0,sQuery(id+"F6.wireOp",EDGE,"E46.left")]}),-1.0]])],"derivedFrom":subQ0})])],"isStart":false});}
            var Q5;
            Q5=makeQuery(id+"F7.opExtrude","CAP_EDGE",EDGE,{"disambiguationData":[OSD([sQuery(id+"F6.wireOp",EDGE,"E45.right")])],"isStart":false});
            var Q6;
            {var subQ0=sQuery(id+"F6.wireOp",EDGE,"E45.top");Q6=makeQuery(id+"F7.opExtrude","CAP_EDGE",EDGE,{"disambiguationData":[OSD([subQ0]),TDD([makeQuery(id+"F6.imprint","IMPRINT",EDGE,{"disambiguationData":[TD([[makeQuery(id+"F6.imprint","INTERSECT",VERTEX,{"derivedFrom":[subQ0,sQuery(id+"F6.wireOp",EDGE,"E46.left")]}),-1.0]])],"derivedFrom":subQ0})])],"isStart":false});}
            var Q7;
            {var subQ0=sQuery(id+"F6.wireOp",EDGE,"E46.left");Q7=makeQuery(id+"F7.opExtrude","CAP_EDGE",EDGE,{"disambiguationData":[OSD([subQ0]),TDD([makeQuery(id+"F6.imprint","IMPRINT",EDGE,{"disambiguationData":[TD([[makeQuery(id+"F6.imprint","INTERSECT",VERTEX,{"derivedFrom":[sQuery(id+"F6.wireOp",EDGE,"E45.top"),subQ0]}),-1.0]])],"derivedFrom":subQ0})])],"isStart":false});}
            var Q8;
            Q8=makeQuery(id+"F7.opExtrude","CAP_EDGE",EDGE,{"disambiguationData":[OSD([sQuery(id+"F6.wireOp",EDGE,"E46.top")])],"isStart":false});
            var Q9;
            {var subQ0=sQuery(id+"F6.wireOp",EDGE,"E46.right");Q9=makeQuery(id+"F7.opExtrude","CAP_EDGE",EDGE,{"disambiguationData":[OSD([subQ0]),TDD([makeQuery(id+"F6.imprint","IMPRINT",EDGE,{"disambiguationData":[TD([[makeQuery(id+"F6.imprint","INTERSECT",VERTEX,{"derivedFrom":[sQuery(id+"F6.wireOp",EDGE,"E45.top"),subQ0]}),-1.0]])],"derivedFrom":subQ0})])],"isStart":false});}
            var Q10;
            {var subQ0=sQuery(id+"F6.wireOp",EDGE,"E45.top");Q10=makeQuery(id+"F7.opExtrude","CAP_EDGE",EDGE,{"disambiguationData":[OSD([subQ0]),TDD([makeQuery(id+"F6.imprint","IMPRINT",EDGE,{"disambiguationData":[TD([[makeQuery(id+"F6.imprint","INTERSECT",VERTEX,{"derivedFrom":[subQ0,sQuery(id+"F6.wireOp",EDGE,"E46.right")]}),1.0]])],"derivedFrom":subQ0})])],"isStart":false});}
            var Q11;
            Q11=makeQuery(id+"F7.opExtrude","CAP_EDGE",EDGE,{"disambiguationData":[OSD([sQuery(id+"F6.wireOp",EDGE,"E45.left")])],"isStart":false});
            var Q12;
            {var subQ0=sQuery(id+"F6.wireOp",EDGE,"E47.right");var subQ1=sQuery(id+"F2.wireOp",EDGE,"E4.bottom");Q12=makeQuery(id+"F7.opExtrude","CAP_EDGE",EDGE,{"disambiguationData":[OSD([subQ0]),TDD([makeQuery(id+"F6.imprint","IMPRINT",EDGE,{"disambiguationData":[TD([[makeQuery(id+"F6.imprint","INTERSECT",VERTEX,{"derivedFrom":[makeQuery(id+"F3.boolean.opBoolean","COPY",EDGE,{"derivedFrom":makeQuery(id+"F3.opExtrude","CAP_EDGE",EDGE,{"disambiguationData":[OSD([subQ1]),TDD([makeQuery(id+"F2.imprint","IMPRINT",EDGE,{"disambiguationData":[TD([[makeQuery(id+"F2.imprint","INTERSECT",VERTEX,{"derivedFrom":[subQ1,sQuery(id+"F2.wireOp",EDGE,"E9")]}),1.0]])],"derivedFrom":subQ1})])],"isStart":true})}),sQuery(id+"F6.wireOp",EDGE,"E47.bottom"),subQ0]}),1.0],[makeQuery(id+"F6.imprint","INTERSECT",VERTEX,{"derivedFrom":[subQ0,sQuery(id+"F6.wireOp",EDGE,"E48.top")]}),-1.0]])],"derivedFrom":subQ0})])],"isStart":false});}
            var Q13;
            {var subQ0=sQuery(id+"F6.wireOp",EDGE,"E48.top");Q13=makeQuery(id+"F7.opExtrude","CAP_EDGE",EDGE,{"disambiguationData":[OSD([subQ0]),TDD([makeQuery(id+"F6.imprint","IMPRINT",EDGE,{"disambiguationData":[TD([[makeQuery(id+"F6.imprint","INTERSECT",VERTEX,{"derivedFrom":[sQuery(id+"F6.wireOp",EDGE,"E47.right"),subQ0]}),-1.0]])],"derivedFrom":subQ0})])],"isStart":false});}
            var Q14;
            Q14=makeQuery(id+"F7.opExtrude","CAP_EDGE",EDGE,{"disambiguationData":[OSD([sQuery(id+"F6.wireOp",EDGE,"E48.right")])],"isStart":false});
            var Q15;
            {var subQ0=sQuery(id+"F6.wireOp",EDGE,"E48.bottom");Q15=makeQuery(id+"F7.opExtrude","CAP_EDGE",EDGE,{"disambiguationData":[OSD([subQ0]),TDD([makeQuery(id+"F6.imprint","IMPRINT",EDGE,{"disambiguationData":[TD([[makeQuery(id+"F6.imprint","INTERSECT",VERTEX,{"derivedFrom":[sQuery(id+"F6.wireOp",EDGE,"E47.right"),subQ0]}),-1.0]])],"derivedFrom":subQ0})])],"isStart":false});}
            var Q16;
            Q16=makeQuery(id+"F7.opExtrude","CAP_EDGE",EDGE,{"disambiguationData":[OSD([sQuery(id+"F6.wireOp",EDGE,"E47.top")])],"isStart":false});
            var Q17;
            Q17=makeQuery(id+"F7.opExtrude","CAP_EDGE",EDGE,{"disambiguationData":[OSD([sQuery(id+"F6.wireOp",EDGE,"E48.left")])],"isStart":false});
            var Q18;
            {var subQ0=sQuery(id+"F6.wireOp",EDGE,"E48.bottom");Q18=makeQuery(id+"F7.opExtrude","CAP_EDGE",EDGE,{"disambiguationData":[OSD([subQ0]),TDD([makeQuery(id+"F6.imprint","IMPRINT",EDGE,{"disambiguationData":[TD([[makeQuery(id+"F6.imprint","INTERSECT",VERTEX,{"derivedFrom":[sQuery(id+"F6.wireOp",EDGE,"E47.left"),subQ0]}),1.0]])],"derivedFrom":subQ0})])],"isStart":false});}
            var Q19;
            {var subQ0=sQuery(id+"F6.wireOp",EDGE,"E47.left");Q19=makeQuery(id+"F7.opExtrude","CAP_EDGE",EDGE,{"disambiguationData":[OSD([subQ0]),TDD([makeQuery(id+"F6.imprint","IMPRINT",EDGE,{"disambiguationData":[TD([[makeQuery(id+"F6.imprint","INTERSECT",VERTEX,{"derivedFrom":[subQ0,sQuery(id+"F6.wireOp",EDGE,"E48.bottom")]}),-1.0]])],"derivedFrom":subQ0})])],"isStart":false});}
            var Q20;
            {var subQ0=sQuery(id+"F6.wireOp",EDGE,"E48.top");Q20=makeQuery(id+"F7.opExtrude","CAP_EDGE",EDGE,{"disambiguationData":[OSD([subQ0]),TDD([makeQuery(id+"F6.imprint","IMPRINT",EDGE,{"disambiguationData":[TD([[makeQuery(id+"F6.imprint","INTERSECT",VERTEX,{"derivedFrom":[sQuery(id+"F6.wireOp",EDGE,"E47.left"),subQ0]}),1.0]])],"derivedFrom":subQ0})])],"isStart":false});}
            var Q21;
            {var subQ0=sQuery(id+"F6.wireOp",EDGE,"E47.left");var subQ1=sQuery(id+"F2.wireOp",EDGE,"E4.bottom");Q21=makeQuery(id+"F7.opExtrude","CAP_EDGE",EDGE,{"disambiguationData":[OSD([subQ0]),TDD([makeQuery(id+"F6.imprint","IMPRINT",EDGE,{"disambiguationData":[TD([[makeQuery(id+"F6.imprint","INTERSECT",VERTEX,{"derivedFrom":[makeQuery(id+"F3.boolean.opBoolean","COPY",EDGE,{"derivedFrom":makeQuery(id+"F3.opExtrude","CAP_EDGE",EDGE,{"disambiguationData":[OSD([subQ1]),TDD([makeQuery(id+"F2.imprint","IMPRINT",EDGE,{"disambiguationData":[TD([[makeQuery(id+"F2.imprint","INTERSECT",VERTEX,{"derivedFrom":[subQ1,sQuery(id+"F2.wireOp",EDGE,"E20")]}),-1.0]])],"derivedFrom":subQ1})])],"isStart":true})}),sQuery(id+"F6.wireOp",EDGE,"E47.bottom"),subQ0]}),1.0]])],"derivedFrom":subQ0})])],"isStart":false});}
            var Q22;
            Q22=makeQuery(id+"F7.opExtrude","CAP_EDGE",EDGE,{"disambiguationData":[OSD([sQuery(id+"F6.wireOp",EDGE,"E47.bottom")])],"isStart":false});
            var Q23;
            Q23=makeQuery(id+"F7.opExtrude","CAP_FACE",FACE,{"disambiguationData":[OSD([sQuery(id+"F6.wireOp",EDGE,"E47.bottom"),sQuery(id+"F6.wireOp",EDGE,"E47.top"),sQuery(id+"F6.wireOp",EDGE,"E47.left"),sQuery(id+"F6.wireOp",EDGE,"E47.right"),sQuery(id+"F6.wireOp",EDGE,"E48.bottom"),sQuery(id+"F6.wireOp",EDGE,"E48.top"),sQuery(id+"F6.wireOp",EDGE,"E48.left"),sQuery(id+"F6.wireOp",EDGE,"E48.right")])],"isStart":false});
            var Q24;
            {var subQ0=sQuery(id+"F6.wireOp",EDGE,"E50.left");Q24=makeQuery(id+"F7.opExtrude","CAP_EDGE",EDGE,{"disambiguationData":[OSD([subQ0]),TDD([makeQuery(id+"F6.imprint","IMPRINT",EDGE,{"disambiguationData":[TD([[makeQuery(id+"F6.imprint","INTERSECT",VERTEX,{"derivedFrom":[sQuery(id+"F6.wireOp",EDGE,"E49.bottom"),subQ0]}),-1.0]])],"derivedFrom":subQ0})])],"isStart":false});}
            var Q25;
            {var subQ0=sQuery(id+"F6.wireOp",EDGE,"E50.left");Q25=makeQuery(id+"F7.opExtrude","CAP_EDGE",EDGE,{"disambiguationData":[OSD([subQ0]),TDD([makeQuery(id+"F6.imprint","IMPRINT",EDGE,{"disambiguationData":[TD([[makeQuery(id+"F6.imprint","INTERSECT",VERTEX,{"derivedFrom":[sQuery(id+"F6.wireOp",EDGE,"E49.top"),subQ0]}),1.0]])],"derivedFrom":subQ0})])],"isStart":false});}
            var Q26;
            Q26=makeQuery(id+"F7.opExtrude","CAP_EDGE",EDGE,{"disambiguationData":[OSD([sQuery(id+"F6.wireOp",EDGE,"E50.bottom")])],"isStart":false});
            var Q27;
            {var subQ0=sQuery(id+"F6.wireOp",EDGE,"E50.right");Q27=makeQuery(id+"F7.opExtrude","CAP_EDGE",EDGE,{"disambiguationData":[OSD([subQ0]),TDD([makeQuery(id+"F6.imprint","IMPRINT",EDGE,{"disambiguationData":[TD([[makeQuery(id+"F6.imprint","INTERSECT",VERTEX,{"derivedFrom":[sQuery(id+"F6.wireOp",EDGE,"E49.top"),subQ0]}),1.0]])],"derivedFrom":subQ0})])],"isStart":false});}
            var Q28;
            {var subQ0=sQuery(id+"F6.wireOp",EDGE,"E49.top");Q28=makeQuery(id+"F7.opExtrude","CAP_EDGE",EDGE,{"disambiguationData":[OSD([subQ0]),TDD([makeQuery(id+"F6.imprint","IMPRINT",EDGE,{"disambiguationData":[TD([[makeQuery(id+"F6.imprint","INTERSECT",VERTEX,{"derivedFrom":[subQ0,sQuery(id+"F6.wireOp",EDGE,"E50.right")]}),1.0]])],"derivedFrom":subQ0})])],"isStart":false});}
            var Q29;
            Q29=makeQuery(id+"F7.opExtrude","CAP_EDGE",EDGE,{"disambiguationData":[OSD([sQuery(id+"F6.wireOp",EDGE,"E49.left")])],"isStart":false});
            var Q30;
            {var subQ0=sQuery(id+"F6.wireOp",EDGE,"E49.bottom");Q30=makeQuery(id+"F7.opExtrude","CAP_EDGE",EDGE,{"disambiguationData":[OSD([subQ0]),TDD([makeQuery(id+"F6.imprint","IMPRINT",EDGE,{"disambiguationData":[TD([[makeQuery(id+"F6.imprint","INTERSECT",VERTEX,{"derivedFrom":[subQ0,sQuery(id+"F6.wireOp",EDGE,"E50.right")]}),1.0]])],"derivedFrom":subQ0})])],"isStart":false});}
            var Q31;
            {var subQ0=sQuery(id+"F6.wireOp",EDGE,"E50.right");Q31=makeQuery(id+"F7.opExtrude","CAP_EDGE",EDGE,{"disambiguationData":[OSD([subQ0]),TDD([makeQuery(id+"F6.imprint","IMPRINT",EDGE,{"disambiguationData":[TD([[makeQuery(id+"F6.imprint","INTERSECT",VERTEX,{"derivedFrom":[sQuery(id+"F6.wireOp",EDGE,"E49.bottom"),subQ0]}),-1.0]])],"derivedFrom":subQ0})])],"isStart":false});}
            var Q32;
            Q32=makeQuery(id+"F7.opExtrude","CAP_EDGE",EDGE,{"disambiguationData":[OSD([sQuery(id+"F6.wireOp",EDGE,"E50.top")])],"isStart":false});
            var Q33;
            {var subQ0=sQuery(id+"F6.wireOp",EDGE,"E49.bottom");Q33=makeQuery(id+"F7.opExtrude","CAP_EDGE",EDGE,{"disambiguationData":[OSD([subQ0]),TDD([makeQuery(id+"F6.imprint","IMPRINT",EDGE,{"disambiguationData":[TD([[makeQuery(id+"F6.imprint","INTERSECT",VERTEX,{"derivedFrom":[subQ0,sQuery(id+"F6.wireOp",EDGE,"E50.left")]}),-1.0]])],"derivedFrom":subQ0})])],"isStart":false});}
            var Q34;
            {var subQ0=sQuery(id+"F6.wireOp",EDGE,"E49.top");Q34=makeQuery(id+"F7.opExtrude","CAP_EDGE",EDGE,{"disambiguationData":[OSD([subQ0]),TDD([makeQuery(id+"F6.imprint","IMPRINT",EDGE,{"disambiguationData":[TD([[makeQuery(id+"F6.imprint","INTERSECT",VERTEX,{"derivedFrom":[subQ0,sQuery(id+"F6.wireOp",EDGE,"E50.left")]}),-1.0]])],"derivedFrom":subQ0})])],"isStart":false});}
            var Q35;
            Q35=makeQuery(id+"F7.opExtrude","CAP_EDGE",EDGE,{"disambiguationData":[OSD([sQuery(id+"F6.wireOp",EDGE,"E42.left")])],"isStart":false});
            var Q36;
            {var subQ0=sQuery(id+"F6.wireOp",EDGE,"E52.bottom");Q36=makeQuery(id+"F7.opExtrude","CAP_EDGE",EDGE,{"disambiguationData":[OSD([subQ0]),TDD([makeQuery(id+"F6.imprint","IMPRINT",EDGE,{"disambiguationData":[TD([[makeQuery(id+"F6.imprint","INTERSECT",VERTEX,{"derivedFrom":[sQuery(id+"F6.wireOp",EDGE,"E51.right"),subQ0]}),1.0],[makeQuery(id+"F6.imprint","INTERSECT",VERTEX,{"derivedFrom":[sQuery(id+"F6.wireOp",EDGE,"E41.top"),subQ0,sQuery(id+"F6.wireOp",EDGE,"E52.right")]}),-1.0]])],"derivedFrom":subQ0})])],"isStart":false});}
            var Q37;
            {var subQ0=sQuery(id+"F6.wireOp",EDGE,"E51.right");Q37=makeQuery(id+"F7.opExtrude","CAP_EDGE",EDGE,{"disambiguationData":[OSD([subQ0]),TDD([makeQuery(id+"F6.imprint","IMPRINT",EDGE,{"disambiguationData":[TD([[makeQuery(id+"F6.imprint","INTERSECT",VERTEX,{"derivedFrom":[subQ0,sQuery(id+"F6.wireOp",EDGE,"E52.bottom")]}),-1.0]])],"derivedFrom":subQ0})])],"isStart":false});}
            var Q38;
            Q38=makeQuery(id+"F7.opExtrude","CAP_EDGE",EDGE,{"disambiguationData":[OSD([sQuery(id+"F6.wireOp",EDGE,"E40.bottom")])],"isStart":false});
            var Q39;
            {var subQ0=sQuery(id+"F6.wireOp",EDGE,"E51.left");var subQ1=sQuery(id+"F2.wireOp",EDGE,"E12.top");Q39=makeQuery(id+"F7.opExtrude","CAP_EDGE",EDGE,{"disambiguationData":[OSD([subQ0]),TDD([makeQuery(id+"F6.imprint","IMPRINT",EDGE,{"disambiguationData":[TD([[makeQuery(id+"F6.imprint","INTERSECT",VERTEX,{"derivedFrom":[makeQuery(id+"F3.boolean.opBoolean","COPY",EDGE,{"derivedFrom":makeQuery(id+"F3.opExtrude","CAP_EDGE",EDGE,{"disambiguationData":[OSD([subQ1]),TDD([makeQuery(id+"F2.imprint","IMPRINT",EDGE,{"disambiguationData":[TD([[makeQuery(id+"F2.imprint","INTERSECT",VERTEX,{"derivedFrom":[sQuery(id+"F2.wireOp",EDGE,"E8.right"),subQ1]}),-1.0]])],"derivedFrom":subQ1})])],"isStart":true})}),sQuery(id+"F6.wireOp",EDGE,"E40.left"),sQuery(id+"F6.wireOp",EDGE,"E40.bottom"),subQ0]}),-1.0],[makeQuery(id+"F6.imprint","INTERSECT",VERTEX,{"derivedFrom":[subQ0,sQuery(id+"F6.wireOp",EDGE,"E52.bottom")]}),1.0]])],"derivedFrom":subQ0})])],"isStart":false});}
            var Q40;
            {var subQ0=sQuery(id+"F6.wireOp",EDGE,"E52.bottom");var subQ1=sQuery(id+"F2.wireOp",EDGE,"E8.right");Q40=makeQuery(id+"F7.opExtrude","CAP_EDGE",EDGE,{"disambiguationData":[OSD([subQ0]),TDD([makeQuery(id+"F6.imprint","IMPRINT",EDGE,{"disambiguationData":[TD([[makeQuery(id+"F6.imprint","INTERSECT",VERTEX,{"derivedFrom":[makeQuery(id+"F3.boolean.opBoolean","COPY",EDGE,{"derivedFrom":makeQuery(id+"F3.opExtrude","CAP_EDGE",EDGE,{"disambiguationData":[OSD([subQ1]),TDD([makeQuery(id+"F2.imprint","IMPRINT",EDGE,{"disambiguationData":[TD([[makeQuery(id+"F2.imprint","INTERSECT",VERTEX,{"derivedFrom":[subQ1,sQuery(id+"F2.wireOp",EDGE,"E12.top")]}),-1.0]])],"derivedFrom":subQ1})])],"isStart":true})}),subQ0,sQuery(id+"F6.wireOp",EDGE,"E52.left")]}),1.0],[makeQuery(id+"F6.imprint","INTERSECT",VERTEX,{"derivedFrom":[sQuery(id+"F6.wireOp",EDGE,"E51.left"),subQ0]}),-1.0]])],"derivedFrom":subQ0})])],"isStart":false});}
            var Q41;
            Q41=makeQuery(id+"F7.opExtrude","CAP_EDGE",EDGE,{"disambiguationData":[OSD([sQuery(id+"F6.wireOp",EDGE,"E52.left")])],"isStart":false});
            var Q42;
            {var subQ0=sQuery(id+"F6.wireOp",EDGE,"E51.left");var subQ1=sQuery(id+"F2.wireOp",EDGE,"E4.top");Q42=makeQuery(id+"F7.opExtrude","CAP_EDGE",EDGE,{"disambiguationData":[OSD([subQ0]),TDD([makeQuery(id+"F6.imprint","IMPRINT",EDGE,{"disambiguationData":[TD([[makeQuery(id+"F6.imprint","INTERSECT",VERTEX,{"derivedFrom":[makeQuery(id+"F3.boolean.opBoolean","COPY",EDGE,{"derivedFrom":makeQuery(id+"F3.opExtrude","CAP_EDGE",EDGE,{"disambiguationData":[OSD([subQ1]),TDD([makeQuery(id+"F2.imprint","IMPRINT",EDGE,{"disambiguationData":[TD([[makeQuery(id+"F2.imprint","INTERSECT",VERTEX,{"derivedFrom":[subQ1,sQuery(id+"F2.wireOp",EDGE,"E8.right")]}),-1.0]])],"derivedFrom":subQ1})])],"isStart":true})}),sQuery(id+"F6.wireOp",EDGE,"E51.bottom"),subQ0]}),1.0],[makeQuery(id+"F6.imprint","INTERSECT",VERTEX,{"derivedFrom":[subQ0,sQuery(id+"F6.wireOp",EDGE,"E52.top")]}),-1.0]])],"derivedFrom":subQ0})])],"isStart":false});}
            var Q43;
            {var subQ0=sQuery(id+"F6.wireOp",EDGE,"E52.top");var subQ1=sQuery(id+"F2.wireOp",EDGE,"E8.right");Q43=makeQuery(id+"F7.opExtrude","CAP_EDGE",EDGE,{"disambiguationData":[OSD([subQ0]),TDD([makeQuery(id+"F6.imprint","IMPRINT",EDGE,{"disambiguationData":[TD([[makeQuery(id+"F6.imprint","INTERSECT",VERTEX,{"derivedFrom":[makeQuery(id+"F3.boolean.opBoolean","COPY",EDGE,{"derivedFrom":makeQuery(id+"F3.opExtrude","CAP_EDGE",EDGE,{"disambiguationData":[OSD([subQ1]),TDD([makeQuery(id+"F2.imprint","IMPRINT",EDGE,{"disambiguationData":[TD([[makeQuery(id+"F2.imprint","INTERSECT",VERTEX,{"derivedFrom":[sQuery(id+"F2.wireOp",EDGE,"E4.top"),subQ1]}),1.0]])],"derivedFrom":subQ1})])],"isStart":true})}),subQ0,sQuery(id+"F6.wireOp",EDGE,"E52.left")]}),1.0],[makeQuery(id+"F6.imprint","INTERSECT",VERTEX,{"derivedFrom":[sQuery(id+"F6.wireOp",EDGE,"E51.left"),subQ0]}),-1.0]])],"derivedFrom":subQ0})])],"isStart":false});}
            var Q44;
            Q44=makeQuery(id+"F7.opExtrude","CAP_EDGE",EDGE,{"disambiguationData":[OSD([sQuery(id+"F6.wireOp",EDGE,"E51.bottom")])],"isStart":false});
            var Q45;
            {var subQ0=sQuery(id+"F6.wireOp",EDGE,"E52.top");Q45=makeQuery(id+"F7.opExtrude","CAP_EDGE",EDGE,{"disambiguationData":[OSD([subQ0]),TDD([makeQuery(id+"F6.imprint","IMPRINT",EDGE,{"disambiguationData":[TD([[makeQuery(id+"F6.imprint","INTERSECT",VERTEX,{"derivedFrom":[makeQuery(id+"F3.boolean.opBoolean","COPY",EDGE,{"derivedFrom":makeQuery(id+"F3.opExtrude","CAP_EDGE",EDGE,{"disambiguationData":[OSD([sQuery(id+"F2.wireOp",EDGE,"E29.left")])],"isStart":true})}),sQuery(id+"F6.wireOp",EDGE,"E41.bottom"),subQ0,sQuery(id+"F6.wireOp",EDGE,"E52.right")]}),-1.0],[makeQuery(id+"F6.imprint","INTERSECT",VERTEX,{"derivedFrom":[sQuery(id+"F6.wireOp",EDGE,"E51.right"),subQ0]}),1.0]])],"derivedFrom":subQ0})])],"isStart":false});}
            var Q46;
            Q46=makeQuery(id+"F7.opExtrude","CAP_EDGE",EDGE,{"disambiguationData":[OSD([sQuery(id+"F6.wireOp",EDGE,"E52.right")])],"isStart":false});
            var Q47;
            {var subQ0=sQuery(id+"F6.wireOp",EDGE,"E51.right");var subQ1=sQuery(id+"F2.wireOp",EDGE,"E4.top");Q47=makeQuery(id+"F7.opExtrude","CAP_EDGE",EDGE,{"disambiguationData":[OSD([subQ0]),TDD([makeQuery(id+"F6.imprint","IMPRINT",EDGE,{"disambiguationData":[TD([[makeQuery(id+"F6.imprint","INTERSECT",VERTEX,{"derivedFrom":[makeQuery(id+"F3.boolean.opBoolean","COPY",EDGE,{"derivedFrom":makeQuery(id+"F3.opExtrude","CAP_EDGE",EDGE,{"disambiguationData":[OSD([subQ1]),TDD([makeQuery(id+"F2.imprint","IMPRINT",EDGE,{"disambiguationData":[TD([[makeQuery(id+"F2.imprint","INTERSECT",VERTEX,{"derivedFrom":[subQ1,sQuery(id+"F2.wireOp",EDGE,"E21.top"),sQuery(id+"F2.wireOp",EDGE,"E21.left")]}),-1.0]])],"derivedFrom":subQ1})])],"isStart":true})}),sQuery(id+"F6.wireOp",EDGE,"E51.bottom"),subQ0]}),1.0]])],"derivedFrom":subQ0})])],"isStart":false});}
            chamfer(context, id + "F8", {"entities" : qUnion([Q0, Q1, Q2, Q3, Q4, Q5, Q6, Q7, Q8, Q9, Q10, Q11, Q12, Q13, Q14, Q15, Q16, Q17, Q18, Q19, Q20, Q21, Q22, Q23, Q24, Q25, Q26, Q27, Q28, Q29, Q30, Q31, Q32, Q33, Q34, Q35, Q36, Q37, Q38, Q39, Q40, Q41, Q42, Q43, Q44, Q45, Q46, Q47]), "width" : 1.27 * mm, "tangentPropagation" : true});
        }
        {
            var Q0;
            Q0=makeQuery(id+"F1.opExtrude","CAP_FACE",FACE,{"disambiguationData":[OSD([sQuery(id+"F0.wireOp",EDGE,"E1")])],"isStart":false});
            var sketch = newSketch(context, id + "F9", { "sketchPlane" : qUnion([Q0])});
            skLineSegment(sketch, "E53.bottom", {"start": v(13.67, 49.13) * mm, "end": v(-6.44, 49.13) * mm});
            skLineSegment(sketch, "E53.left", {"start": v(13.67, 49.13) * mm, "end": v(13.67, 59.18) * mm});
            skLineSegment(sketch, "E53.right", {"start": v(-6.44, 49.13) * mm, "end": v(-6.44, 59.18) * mm});
            skPoint(sketch, "E53.middle", {"position": v(3.62, 59.18) * mm});
            skPoint(sketch, "E53.top.end.orphan", {"position": v(-6.44, 69.24) * mm});
            skPoint(sketch, "E54.end.orphan", {"position": v(13.67, 69.24) * mm});
            skSolve(sketch);
        }
        {
            var Q0;
            {var subQ0=sQuery(id+"F9.wireOp",EDGE,"E53.right");Q0=makeQuery(id+"F9.imprint","IMPRINT",FACE,{"disambiguationData":[TD([[makeQuery(id+"F9.imprint","IMPRINT",EDGE,{"derivedFrom":subQ0}),-1.0]])]});}
            var Q1;
            {var subQ0=sQuery(id+"F9.wireOp",EDGE,"E53.left");Q1=makeQuery(id+"F9.imprint","IMPRINT",FACE,{"disambiguationData":[TD([[makeQuery(id+"F9.imprint","IMPRINT",EDGE,{"derivedFrom":subQ0}),1.0]])]});}
            extrude(context, id + "F10", {"entities" : qUnion([Q0, Q1]), "depth" : -6.35 * mm, "offsetDistance" : 25.4 * mm});
        }
    });
